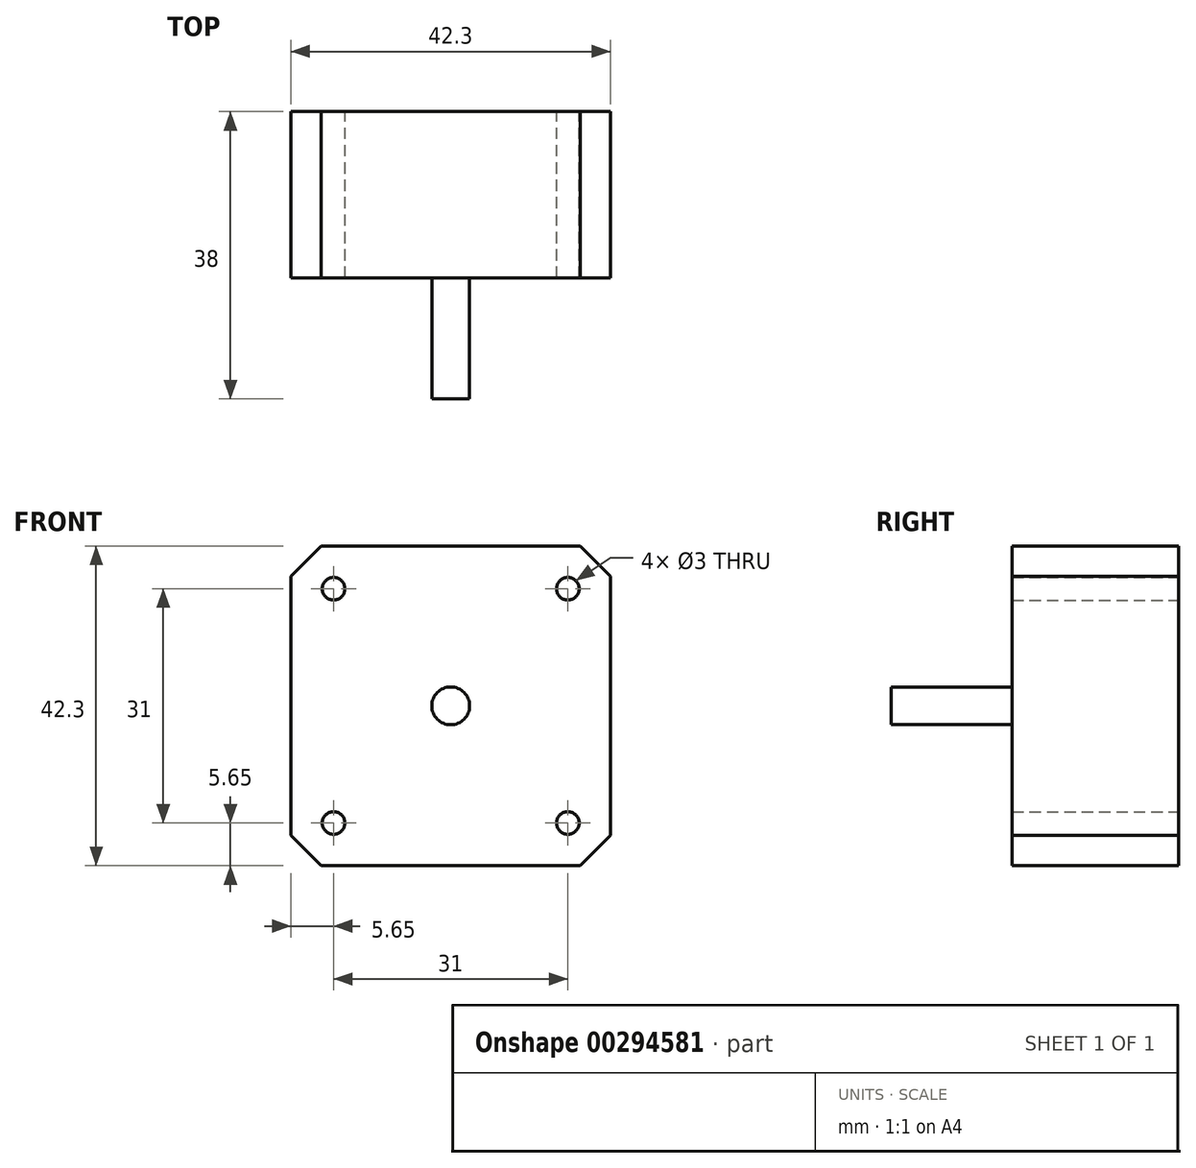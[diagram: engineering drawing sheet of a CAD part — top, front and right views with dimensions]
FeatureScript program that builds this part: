
annotation { "Feature Type Name" : "Feature", "Feature Type Description" : "" }
export const myFeature = defineFeature(function(context is Context, id is Id, definition is map)
    precondition{}
    {
        {
            var Q0;
            Q0=qCreatedBy(makeId("Front.planeOp"),FACE);
            var sketch = newSketch(context, id + "F0", { "sketchPlane" : qUnion([Q0])});
            skLineSegment(sketch, "E0.bottom", {"start": v(-21.15, 21.15) * mm, "end": v(21.15, 21.15) * mm});
            skLineSegment(sketch, "E0.top", {"start": v(-21.15, -21.15) * mm, "end": v(21.15, -21.15) * mm});
            skLineSegment(sketch, "E0.left", {"start": v(-21.15, 21.15) * mm, "end": v(-21.15, -21.15) * mm});
            skLineSegment(sketch, "E0.right", {"start": v(21.15, 21.15) * mm, "end": v(21.15, -21.15) * mm});
            skLineSegment(sketch, "E1.bottom", {"start": v(-15.5, 15.5) * mm, "end": v(15.5, 15.5) * mm, "construction": true});
            skLineSegment(sketch, "E1.top", {"start": v(-15.5, -15.5) * mm, "end": v(15.5, -15.5) * mm, "construction": true});
            skLineSegment(sketch, "E1.left", {"start": v(-15.5, 15.5) * mm, "end": v(-15.5, -15.5) * mm, "construction": true});
            skLineSegment(sketch, "E1.right", {"start": v(15.5, 15.5) * mm, "end": v(15.5, -15.5) * mm, "construction": true});
            skCircle(sketch, "E2", {"center": v(-15.5, 15.5) * mm, "radius": 1.5 * mm});
            skCircle(sketch, "E3", {"center": v(15.5, 15.5) * mm, "radius": 1.5 * mm});
            skCircle(sketch, "E4", {"center": v(15.5, -15.5) * mm, "radius": 1.5 * mm});
            skCircle(sketch, "E5", {"center": v(-15.5, -15.5) * mm, "radius": 1.5 * mm});
            skSolve(sketch);
        }
        {
            var Q0;
            Q0=qSketchRegion(id+"F0",true);
            extrude(context, id + "F1", {"entities" : qUnion([Q0]), "depth" : 22 * mm});
        }
        {
            var Q0;
            Q0=makeQuery(id+"F1.opExtrude","CAP_FACE",FACE,{"disambiguationData":[OSD([sQuery(id+"F0.wireOp",EDGE,"E0.bottom"),sQuery(id+"F0.wireOp",EDGE,"E0.top"),sQuery(id+"F0.wireOp",EDGE,"E0.left"),sQuery(id+"F0.wireOp",EDGE,"E0.right"),sQuery(id+"F0.wireOp",EDGE,"E2"),sQuery(id+"F0.wireOp",EDGE,"E3"),sQuery(id+"F0.wireOp",EDGE,"E4"),sQuery(id+"F0.wireOp",EDGE,"E5")])],"isStart":false});
            var sketch = newSketch(context, id + "F2", { "sketchPlane" : qUnion([Q0])});
            skCircle(sketch, "E6", {"center": v(0, 0) * mm, "radius": 2.5 * mm});
            skSolve(sketch);
        }
        {
            var Q0;
            Q0=qSketchRegion(id+"F2",true);
            extrude(context, id + "F3", {"entities" : qUnion([Q0]), "operationType" : NewBodyOperationType.ADD, "depth" : 16 * mm});
        }
        {
            var Q0;
            Q0=makeQuery(id+"F1.opExtrude","SWEPT_EDGE",EDGE,{"disambiguationData":[OSD([sQuery(id+"F0.wireOp",EDGE,"E0.bottom"),sQuery(id+"F0.wireOp",EDGE,"E0.right")])]});
            var Q1;
            Q1=makeQuery(id+"F1.opExtrude","SWEPT_EDGE",EDGE,{"disambiguationData":[OSD([sQuery(id+"F0.wireOp",EDGE,"E0.top"),sQuery(id+"F0.wireOp",EDGE,"E0.right")])]});
            var Q2;
            Q2=makeQuery(id+"F1.opExtrude","SWEPT_EDGE",EDGE,{"disambiguationData":[OSD([sQuery(id+"F0.wireOp",EDGE,"E0.bottom"),sQuery(id+"F0.wireOp",EDGE,"E0.left")])]});
            var Q3;
            Q3=makeQuery(id+"F1.opExtrude","SWEPT_EDGE",EDGE,{"disambiguationData":[OSD([sQuery(id+"F0.wireOp",EDGE,"E0.top"),sQuery(id+"F0.wireOp",EDGE,"E0.left")])]});
            chamfer(context, id + "F4", {"entities" : qUnion([Q0, Q1, Q2, Q3]), "width" : 4 * mm, "tangentPropagation" : true});
        }
    });
